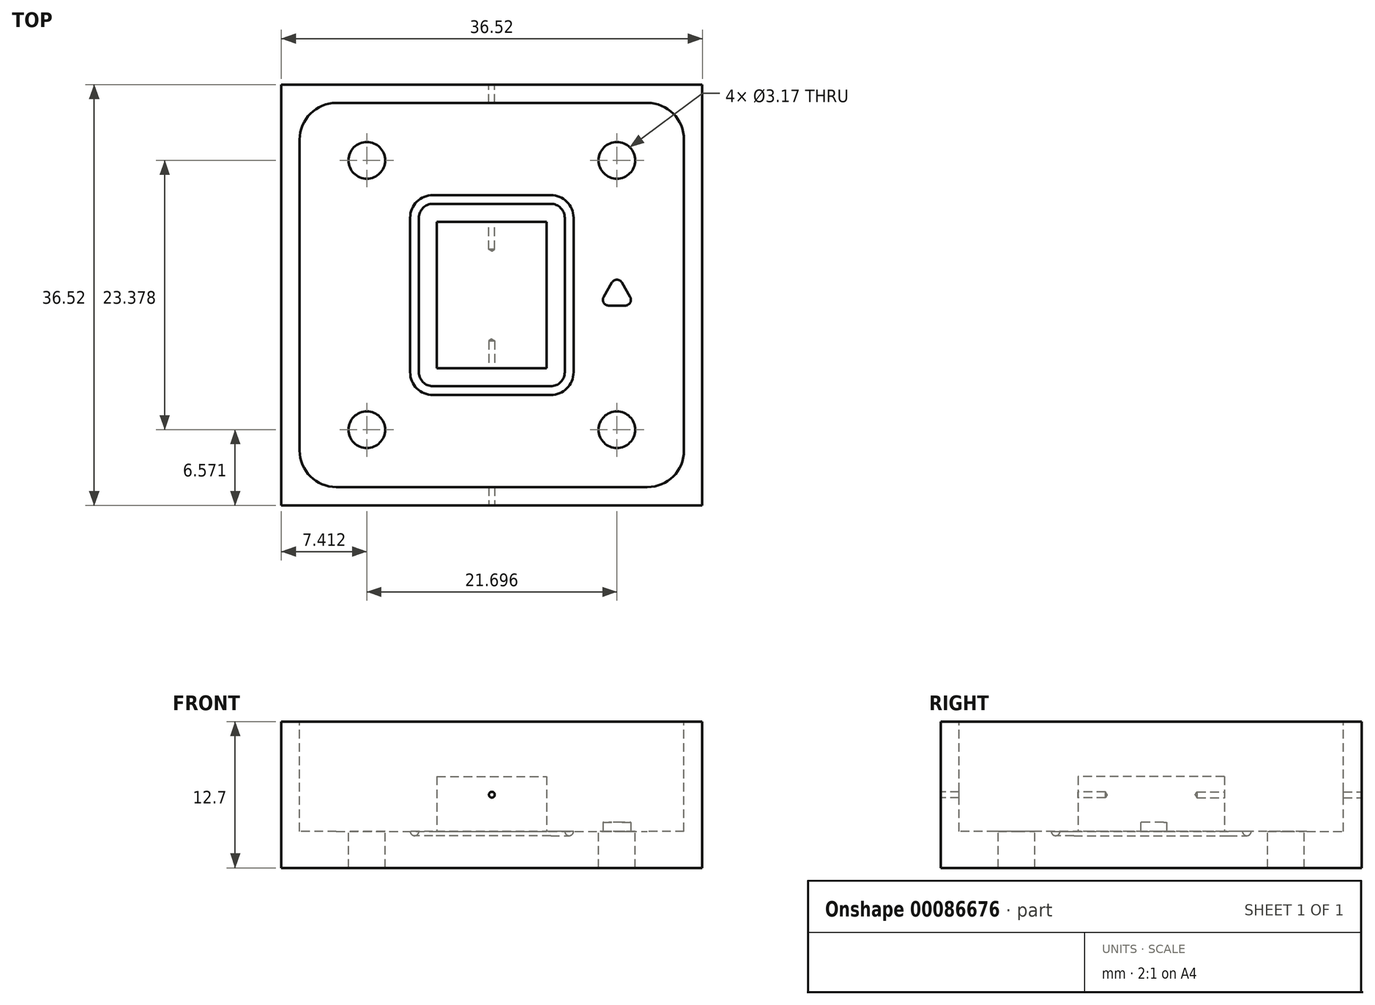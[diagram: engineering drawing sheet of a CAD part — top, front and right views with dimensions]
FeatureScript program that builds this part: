
annotation { "Feature Type Name" : "Feature", "Feature Type Description" : "" }
export const myFeature = defineFeature(function(context is Context, id is Id, definition is map)
    precondition{}
    {
        {
            var Q0;
            Q0=qCreatedBy(makeId("Top.planeOp"),FACE);
            var sketch = newSketch(context, id + "F0", { "sketchPlane" : qUnion([Q0])});
            skLineSegment(sketch, "E0.bottom", {"start": v(-18.26, 18.26) * mm, "end": v(18.26, 18.26) * mm});
            skLineSegment(sketch, "E0.top", {"start": v(-18.26, -18.26) * mm, "end": v(18.26, -18.26) * mm});
            skLineSegment(sketch, "E0.left", {"start": v(-18.26, 18.26) * mm, "end": v(-18.26, -18.26) * mm});
            skLineSegment(sketch, "E0.right", {"start": v(18.26, 18.26) * mm, "end": v(18.26, -18.26) * mm});
            skLineSegment(sketch, "E1", {"start": v(-18.26, 0) * mm, "end": v(18.26, 0) * mm, "construction": true});
            skSolve(sketch);
        }
        {
            var Q0;
            Q0 = qSketchRegion(id + "F0", true);
            var Q1;
            Q1=makeQuery(id+"F0.imprint","IMPRINT",FACE,{"disambiguationData":[TD([[makeQuery(id+"F0.imprint","IMPRINT",EDGE,{"derivedFrom":sQuery(id+"F0.wireOp",EDGE,"E0.bottom")}),-1.0]])]});
            extrude(context, id + "F1", {"entities" : qUnion([Q0, Q1]), "depth" : 12.7 * mm});
        }
        {
            var Q0;
            Q0=makeQuery(id+"F1.opExtrude","CAP_FACE",FACE,{"disambiguationData":[OSD([sQuery(id+"F0.wireOp",EDGE,"E0.bottom"),sQuery(id+"F0.wireOp",EDGE,"E0.top"),sQuery(id+"F0.wireOp",EDGE,"E0.left"),sQuery(id+"F0.wireOp",EDGE,"E0.right")])],"isStart":false});
            var sketch = newSketch(context, id + "F2", { "sketchPlane" : qUnion([Q0])});
            skLineSegment(sketch, "E2.bottom", {"start": v(-16.67, 16.67) * mm, "end": v(16.67, 16.67) * mm});
            skLineSegment(sketch, "E2.top", {"start": v(-16.67, -16.67) * mm, "end": v(16.67, -16.67) * mm});
            skLineSegment(sketch, "E2.left", {"start": v(-16.67, 16.67) * mm, "end": v(-16.67, -16.67) * mm});
            skLineSegment(sketch, "E2.right", {"start": v(16.67, 16.67) * mm, "end": v(16.67, -16.67) * mm});
            skLineSegment(sketch, "E3", {"start": v(-16.67, 0) * mm, "end": v(16.67, 0) * mm, "construction": true});
            skSolve(sketch);
        }
        {
            var Q0;
            Q0 = qSketchRegion(id + "F2", true);
            extrude(context, id + "F3", {"entities" : qUnion([Q0]), "operationType" : NewBodyOperationType.REMOVE, "oppositeDirection" : true, "depth" : 9.52 * mm});
        }
        {
            var Q0;
            Q0=makeQuery(id+"F3.boolean.opBoolean","COPY",FACE,{"derivedFrom":makeQuery(id+"F3.opExtrude","CAP_FACE",FACE,{"disambiguationData":[OSD([sQuery(id+"F2.wireOp",EDGE,"E2.bottom"),sQuery(id+"F2.wireOp",EDGE,"E2.top"),sQuery(id+"F2.wireOp",EDGE,"E2.left"),sQuery(id+"F2.wireOp",EDGE,"E2.right")])],"isStart":false})});
            var sketch = newSketch(context, id + "F4", { "sketchPlane" : qUnion([Q0])});
            skLineSegment(sketch, "E4.bottom", {"start": v(-4.76, 6.35) * mm, "end": v(4.76, 6.35) * mm});
            skLineSegment(sketch, "E4.top", {"start": v(-4.76, -6.35) * mm, "end": v(4.76, -6.35) * mm});
            skLineSegment(sketch, "E4.left", {"start": v(-4.76, 6.35) * mm, "end": v(-4.76, -6.35) * mm});
            skLineSegment(sketch, "E4.right", {"start": v(4.76, 6.35) * mm, "end": v(4.76, -6.35) * mm});
            skLineSegment(sketch, "E5", {"start": v(-4.76, 0) * mm, "end": v(4.76, 0) * mm, "construction": true});
            skSolve(sketch);
        }
        {
            var Q0;
            Q0 = qSketchRegion(id + "F4", true);
            extrude(context, id + "F5", {"entities" : qUnion([Q0]), "operationType" : NewBodyOperationType.ADD, "depth" : 4.76 * mm});
        }
        {
            var Q0;
            Q0=makeQuery(id+"F1.opExtrude","SWEPT_FACE",FACE,{"disambiguationData":[OSD([sQuery(id+"F0.wireOp",EDGE,"E0.top")])]});
            var sketch = newSketch(context, id + "F6", { "sketchPlane" : qUnion([Q0])});
            skLineSegment(sketch, "E6", {"start": v(0, 12.7) * mm, "end": v(0, 6.35) * mm, "construction": true});
            skPoint(sketch, "E6.endSnap0", {"position": v(0, 12.7) * mm});
            skSolve(sketch);
        }
        {
            var Q0;
            Q0=sQuery(id+"F6.wireOp",VERTEX,"E6.end");
            var Q1;
            Q1=makeQuery(id+"F1.opExtrude","SWEPT_BODY",BODY,{"disambiguationData":[OSD([sQuery(id+"F0.wireOp",EDGE,"E0.bottom"),sQuery(id+"F0.wireOp",EDGE,"E0.top"),sQuery(id+"F0.wireOp",EDGE,"E0.left"),sQuery(id+"F0.wireOp",EDGE,"E0.right")])]});
            hole(context, id + "F7", {"style" : HoleStyle.SIMPLE, "endStyle" : HoleEndStyle.BLIND, "holeDiameter" : 0.5 * mm, "holeDepth" : 14.29 * mm, "locations" : qUnion([Q0]), "scope" : qUnion([Q1])});
        }
        {
            var Q0;
            Q0=makeQuery(id+"F1.opExtrude","SWEPT_FACE",FACE,{"disambiguationData":[OSD([sQuery(id+"F0.wireOp",EDGE,"E0.bottom")])]});
            var sketch = newSketch(context, id + "F8", { "sketchPlane" : qUnion([Q0])});
            skLineSegment(sketch, "E7", {"start": v(0, 12.7) * mm, "end": v(0, 6.35) * mm, "construction": true});
            skPoint(sketch, "E7.endSnap0", {"position": v(0, 12.7) * mm});
            skSolve(sketch);
        }
        {
            var Q0;
            Q0=sQuery(id+"F8.wireOp",VERTEX,"E7.end");
            var Q1;
            Q1=makeQuery(id+"F1.opExtrude","SWEPT_BODY",BODY,{"disambiguationData":[OSD([sQuery(id+"F0.wireOp",EDGE,"E0.bottom"),sQuery(id+"F0.wireOp",EDGE,"E0.top"),sQuery(id+"F0.wireOp",EDGE,"E0.left"),sQuery(id+"F0.wireOp",EDGE,"E0.right")])]});
            hole(context, id + "F9", {"style" : HoleStyle.SIMPLE, "endStyle" : HoleEndStyle.BLIND, "holeDiameter" : 0.5 * mm, "holeDepth" : 14.29 * mm, "locations" : qUnion([Q0]), "scope" : qUnion([Q1])});
        }
        {
            var Q0;
            Q0=makeQuery(id+"F3.boolean.opBoolean","COPY",EDGE,{"derivedFrom":makeQuery(id+"F3.opExtrude","SWEPT_EDGE",EDGE,{"disambiguationData":[OSD([sQuery(id+"F2.wireOp",EDGE,"E2.bottom"),sQuery(id+"F2.wireOp",EDGE,"E2.left")])]})});
            var Q1;
            Q1=makeQuery(id+"F3.boolean.opBoolean","COPY",EDGE,{"derivedFrom":makeQuery(id+"F3.opExtrude","SWEPT_EDGE",EDGE,{"disambiguationData":[OSD([sQuery(id+"F2.wireOp",EDGE,"E2.top"),sQuery(id+"F2.wireOp",EDGE,"E2.left")])]})});
            var Q2;
            Q2=makeQuery(id+"F3.boolean.opBoolean","COPY",EDGE,{"derivedFrom":makeQuery(id+"F3.opExtrude","SWEPT_EDGE",EDGE,{"disambiguationData":[OSD([sQuery(id+"F2.wireOp",EDGE,"E2.top"),sQuery(id+"F2.wireOp",EDGE,"E2.right")])]})});
            var Q3;
            Q3=makeQuery(id+"F3.boolean.opBoolean","COPY",EDGE,{"derivedFrom":makeQuery(id+"F3.opExtrude","SWEPT_EDGE",EDGE,{"disambiguationData":[OSD([sQuery(id+"F2.wireOp",EDGE,"E2.bottom"),sQuery(id+"F2.wireOp",EDGE,"E2.right")])]})});
            fillet(context, id + "F10", {"entities" : qUnion([Q0, Q1, Q2, Q3]), "radius" : 3.17 * mm, "tangentPropagation" : true, "allowEdgeOverflow" : false});
        }
        {
            var Q0;
            Q0=makeQuery(id+"F3.boolean.opBoolean","COPY",FACE,{"derivedFrom":makeQuery(id+"F3.opExtrude","CAP_FACE",FACE,{"disambiguationData":[OSD([sQuery(id+"F2.wireOp",EDGE,"E2.bottom"),sQuery(id+"F2.wireOp",EDGE,"E2.top"),sQuery(id+"F2.wireOp",EDGE,"E2.left"),sQuery(id+"F2.wireOp",EDGE,"E2.right")])],"isStart":false})});
            var sketch = newSketch(context, id + "F11", { "sketchPlane" : qUnion([Q0])});
            skLineSegment(sketch, "E8.bottom", {"start": v(5.12, -8.3) * mm, "end": v(-5.12, -8.3) * mm});
            skLineSegment(sketch, "E8.top", {"start": v(5.12, 8.3) * mm, "end": v(-5.12, 8.3) * mm});
            skLineSegment(sketch, "E8.left", {"start": v(6.7, -6.7) * mm, "end": v(6.7, 6.7) * mm});
            skPoint(sketch, "E8.middle", {"position": v(0, 0) * mm});
            skPoint(sketch, "E9.visualSharp", {"position": v(-6.7, -8.3) * mm});
            skArc(sketch, "E9.filletArc", {"start": v(-6.7, -6.7) * mm, "mid": v(-6.24, -7.83) * mm, "end": v(-5.12, -8.3) * mm});
            skPoint(sketch, "E10.visualSharp", {"position": v(-6.7, 8.3) * mm});
            skArc(sketch, "E10.filletArc", {"start": v(-5.12, 8.3) * mm, "mid": v(-6.24, 7.83) * mm, "end": v(-6.7, 6.7) * mm});
            skPoint(sketch, "E11.visualSharp", {"position": v(6.7, -8.3) * mm});
            skArc(sketch, "E11.filletArc", {"start": v(5.12, -8.3) * mm, "mid": v(6.24, -7.83) * mm, "end": v(6.7, -6.7) * mm});
            skPoint(sketch, "E12.visualSharp", {"position": v(6.7, 8.3) * mm});
            skArc(sketch, "E12.filletArc", {"start": v(6.7, 6.7) * mm, "mid": v(6.24, 7.83) * mm, "end": v(5.12, 8.3) * mm});
            skLineSegment(sketch, "E13", {"start": v(-6.7, 6.7) * mm, "end": v(-6.7, 0) * mm});
            skLineSegment(sketch, "E14", {"start": v(-6.7, 0) * mm, "end": v(-6.7, -6.7) * mm});
            skSolve(sketch);
        }
        {
            var Q0;
            Q0=qCreatedBy(makeId("Front.planeOp"),FACE);
            var sketch = newSketch(context, id + "F12", { "sketchPlane" : qUnion([Q0])});
            skArc(sketch, "E15", {"start": v(-7.09, 3.18) * mm, "mid": v(-6.7, 2.8) * mm, "end": v(-6.32, 3.18) * mm});
            skLineSegment(sketch, "E16", {"start": v(-7.09, 3.18) * mm, "end": v(-6.32, 3.18) * mm});
            skSolve(sketch);
        }
        {
            var Q0;
            Q0 = qSketchRegion(id + "F12", true);
            var Q1;
            Q1 = qConstructionFilter(qBodyType(qCreatedBy(id + "F11" ,EDGE), BodyType.WIRE), ConstructionObject.NO);
            sweep(context, id + "F13", {"operationType" : NewBodyOperationType.REMOVE, "profiles" : qUnion([Q0]), "path" : qUnion([Q1])});
        }
        {
            var Q0;
            {var subQ1=sQuery(id+"F2.wireOp",EDGE,"E2.right");var subQ2=sQuery(id+"F2.wireOp",EDGE,"E2.bottom");var subQ3=sQuery(id+"F2.wireOp",EDGE,"E2.top");var subQ4=sQuery(id+"F2.wireOp",EDGE,"E2.left");Q0=makeQuery(id+"F13.boolean.opBoolean","SPLIT",FACE,{"disambiguationData":[TD([makeQuery(id+"F3.boolean.opBoolean","COPY",FACE,{"derivedFrom":makeQuery(id+"F3.opExtrude","SWEPT_FACE",FACE,{"disambiguationData":[OSD([subQ2])]})})])],"derivedFrom":makeQuery(id+"F3.boolean.opBoolean","COPY",FACE,{"derivedFrom":makeQuery(id+"F3.opExtrude","CAP_FACE",FACE,{"disambiguationData":[OSD([subQ2,subQ3,subQ4,subQ1])],"isStart":false})})});}
            var sketch = newSketch(context, id + "F14", { "sketchPlane" : qUnion([Q0])});
            skLineSegment(sketch, "E17", {"start": v(-15.74, 15.74) * mm, "end": v(-10.85, 11.69) * mm, "construction": true});
            skLineSegment(sketch, "E18", {"start": v(15.74, 15.74) * mm, "end": v(10.85, 11.69) * mm, "construction": true});
            skLineSegment(sketch, "E19", {"start": v(-15.74, -15.74) * mm, "end": v(-10.85, -11.69) * mm, "construction": true});
            skLineSegment(sketch, "E20", {"start": v(15.74, -15.74) * mm, "end": v(10.85, -11.69) * mm, "construction": true});
            skLineSegment(sketch, "E21", {"start": v(15.74, -15.74) * mm, "end": v(6.51, -8.1) * mm, "construction": true});
            skLineSegment(sketch, "E22", {"start": v(6.51, 8.1) * mm, "end": v(15.74, 15.74) * mm, "construction": true});
            skLineSegment(sketch, "E23", {"start": v(-15.74, 15.74) * mm, "end": v(-6.51, 8.1) * mm, "construction": true});
            skLineSegment(sketch, "E24", {"start": v(-15.74, -15.74) * mm, "end": v(-6.51, -8.1) * mm, "construction": true});
            skSolve(sketch);
        }
        {
            var Q0;
            Q0=sQuery(id+"F14.wireOp",VERTEX,"E20.end");
            var Q1;
            Q1=sQuery(id+"F14.wireOp",VERTEX,"E18.end");
            var Q2;
            Q2=sQuery(id+"F14.wireOp",VERTEX,"E17.end");
            var Q3;
            Q3=sQuery(id+"F14.wireOp",VERTEX,"E19.end");
            var Q4;
            Q4=makeQuery(id+"F1.opExtrude","SWEPT_BODY",BODY,{"disambiguationData":[OSD([sQuery(id+"F0.wireOp",EDGE,"E0.bottom"),sQuery(id+"F0.wireOp",EDGE,"E0.top"),sQuery(id+"F0.wireOp",EDGE,"E0.left"),sQuery(id+"F0.wireOp",EDGE,"E0.right")])]});
            hole(context, id + "F15", {"style" : HoleStyle.SIMPLE, "endStyle" : HoleEndStyle.THROUGH, "holeDiameter" : 3.17 * mm, "locations" : qUnion([Q0, Q1, Q2, Q3]), "scope" : qUnion([Q4]), "isTappedThrough" : true});
        }
        {
            var Q0;
            {var subQ1=sQuery(id+"F2.wireOp",EDGE,"E2.right");var subQ2=sQuery(id+"F2.wireOp",EDGE,"E2.bottom");var subQ3=sQuery(id+"F2.wireOp",EDGE,"E2.top");var subQ4=sQuery(id+"F2.wireOp",EDGE,"E2.left");Q0=makeQuery(id+"F13.boolean.opBoolean","SPLIT",FACE,{"disambiguationData":[TD([makeQuery(id+"F3.boolean.opBoolean","COPY",FACE,{"derivedFrom":makeQuery(id+"F3.opExtrude","SWEPT_FACE",FACE,{"disambiguationData":[OSD([subQ2])]})})])],"derivedFrom":makeQuery(id+"F3.boolean.opBoolean","COPY",FACE,{"derivedFrom":makeQuery(id+"F3.opExtrude","CAP_FACE",FACE,{"disambiguationData":[OSD([subQ2,subQ3,subQ4,subQ1])],"isStart":false})})});}
            var sketch = newSketch(context, id + "F16", { "sketchPlane" : qUnion([Q0])});
            skLineSegment(sketch, "E25", {"start": v(10.85, 11.69) * mm, "end": v(10.85, -11.69) * mm, "construction": true});
            skLineSegment(sketch, "E26", {"start": v(10.85, -11.69) * mm, "end": v(10.85, 0) * mm, "construction": true});
            skCircle(sketch, "E27.cCircle", {"center": v(10.85, 0) * mm, "radius": 0.92 * mm, "construction": true});
            skLineSegment(sketch, "E27.0", {"start": v(12.44, -0.92) * mm, "end": v(9.26, -0.92) * mm});
            skLineSegment(sketch, "E27.1", {"start": v(9.26, -0.92) * mm, "end": v(10.85, 1.83) * mm});
            skLineSegment(sketch, "E27.2", {"start": v(10.85, 1.83) * mm, "end": v(12.44, -0.92) * mm});
            skPoint(sketch, "E27.0.midPoint", {"position": v(10.85, -0.92) * mm});
            skSolve(sketch);
        }
        {
            var Q0;
            Q0=makeQuery(id+"F16.imprint","IMPRINT",FACE,{"disambiguationData":[TD([[makeQuery(id+"F16.imprint","IMPRINT",EDGE,{"derivedFrom":sQuery(id+"F16.wireOp",EDGE,"E27.0")}),-1.0]])]});
            extrude(context, id + "F17", {"entities" : qUnion([Q0]), "operationType" : NewBodyOperationType.ADD, "depth" : 0.8 * mm});
        }
        {
            var Q0;
            Q0=makeQuery(id+"F17.opExtrude","SWEPT_EDGE",EDGE,{"disambiguationData":[OSD([sQuery(id+"F16.wireOp",EDGE,"E27.1"),sQuery(id+"F16.wireOp",EDGE,"E27.2")])]});
            var Q1;
            Q1=makeQuery(id+"F17.opExtrude","SWEPT_EDGE",EDGE,{"disambiguationData":[OSD([sQuery(id+"F16.wireOp",EDGE,"E27.0"),sQuery(id+"F16.wireOp",EDGE,"E27.2")])]});
            var Q2;
            Q2=makeQuery(id+"F17.opExtrude","SWEPT_EDGE",EDGE,{"disambiguationData":[OSD([sQuery(id+"F16.wireOp",EDGE,"E27.0"),sQuery(id+"F16.wireOp",EDGE,"E27.1")])]});
            fillet(context, id + "F18", {"entities" : qUnion([Q0, Q1, Q2]), "radius" : 0.5 * mm, "tangentPropagation" : true, "allowEdgeOverflow" : false});
        }
    });
